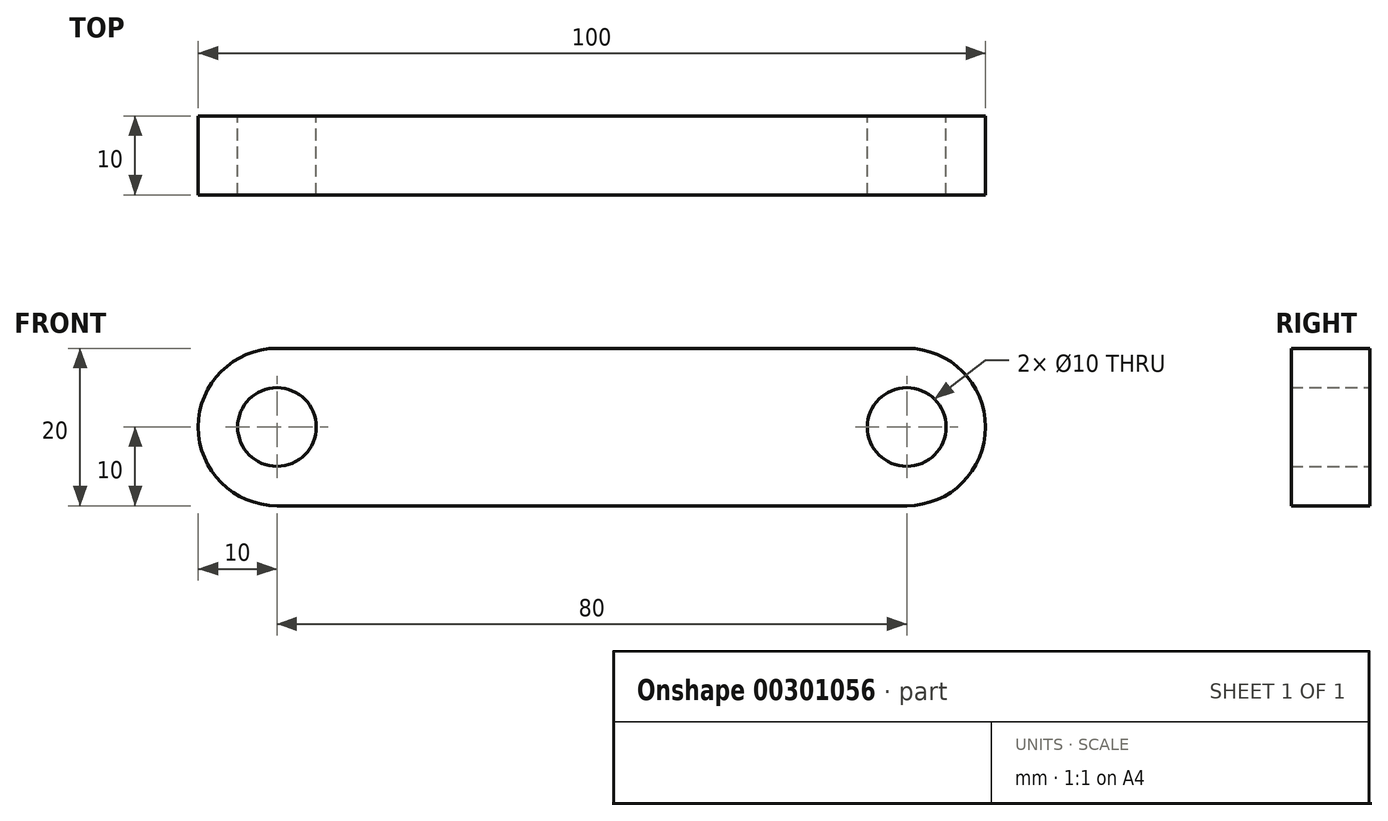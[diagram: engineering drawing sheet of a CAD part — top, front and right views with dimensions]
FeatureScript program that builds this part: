
annotation { "Feature Type Name" : "Feature", "Feature Type Description" : "" }
export const myFeature = defineFeature(function(context is Context, id is Id, definition is map)
    precondition{}
    {
        {
            var Q0;
            Q0=qCreatedBy(makeId("Front.planeOp"),FACE);
            var sketch = newSketch(context, id + "F0", { "sketchPlane" : qUnion([Q0])});
            skLineSegment(sketch, "E0", {"start": v(0, 0) * mm, "end": v(80, 0) * mm});
            skLineSegment(sketch, "E1", {"start": v(0, 20) * mm, "end": v(80, 20) * mm});
            skArc(sketch, "E2", {"start": v(0, 20) * mm, "mid": v(-10, 10) * mm, "end": v(0, 0) * mm});
            skArc(sketch, "E3", {"start": v(80, 0) * mm, "mid": v(90, 10) * mm, "end": v(80, 20) * mm});
            skCircle(sketch, "E4", {"center": v(0, 10) * mm, "radius": 5 * mm});
            skCircle(sketch, "E5", {"center": v(80, 10) * mm, "radius": 5 * mm});
            skSolve(sketch);
        }
        {
            var Q0;
            Q0=makeQuery(id+"F0.imprint","IMPRINT",FACE,{"disambiguationData":[TD([[makeQuery(id+"F0.imprint","IMPRINT",EDGE,{"derivedFrom":sQuery(id+"F0.wireOp",EDGE,"E0")}),1.0]])]});
            extrude(context, id + "F1", {"entities" : qUnion([Q0]), "depth" : 10 * mm});
        }
    });
